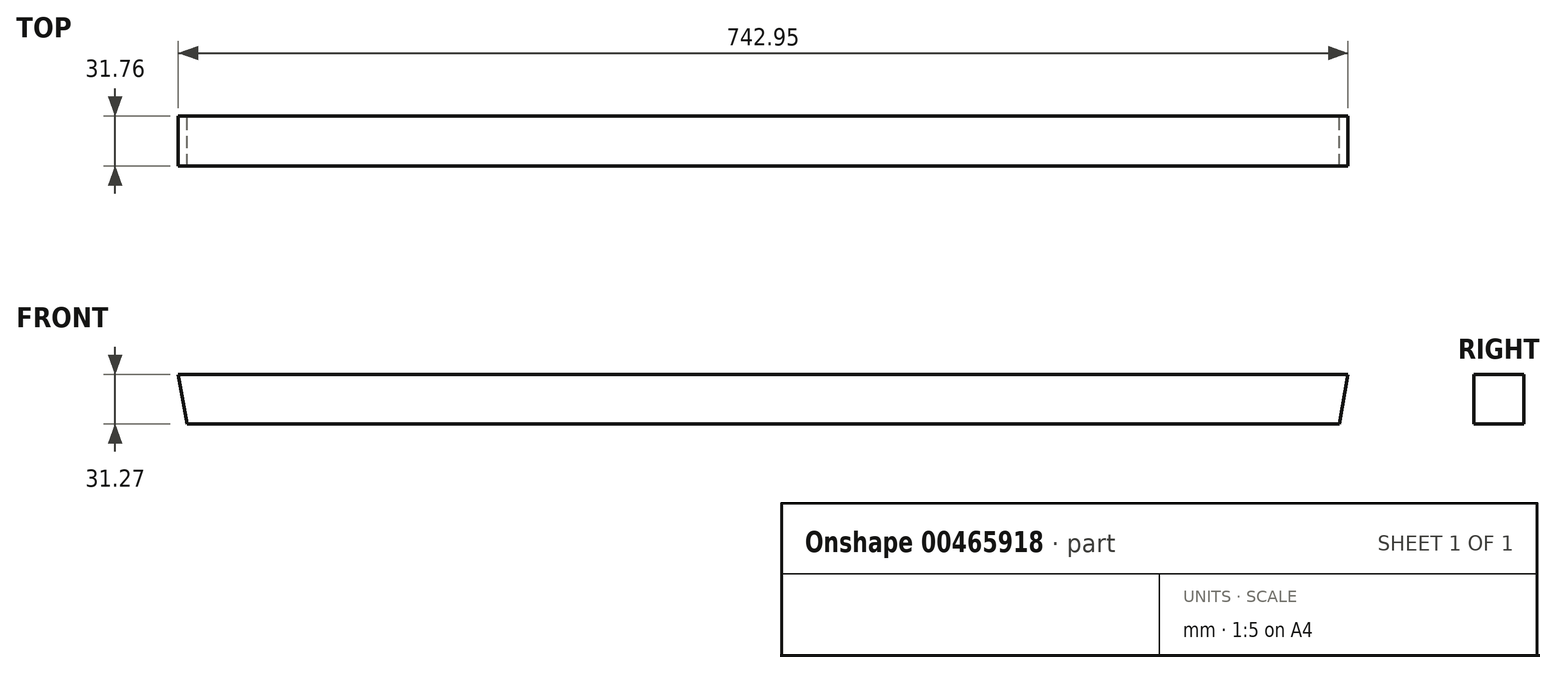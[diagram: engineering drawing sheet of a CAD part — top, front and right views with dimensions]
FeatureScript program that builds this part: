
annotation { "Feature Type Name" : "Feature", "Feature Type Description" : "" }
export const myFeature = defineFeature(function(context is Context, id is Id, definition is map)
    precondition{}
    {
        {
            var Q0;
            Q0=qCreatedBy(makeId("Front.planeOp"),FACE);
            var sketch = newSketch(context, id + "F0", { "sketchPlane" : qUnion([Q0])});
            skLineSegment(sketch, "E0", {"start": v(0, 0) * mm, "end": v(-742.95, 0) * mm});
            skLineSegment(sketch, "E1", {"start": v(-742.95, 0) * mm, "end": v(-737.44, -31.27) * mm});
            skLineSegment(sketch, "E2", {"start": v(0, 0) * mm, "end": v(-5.51, -31.27) * mm});
            skLineSegment(sketch, "E3", {"start": v(-737.44, -31.27) * mm, "end": v(-5.51, -31.27) * mm});
            skSolve(sketch);
        }
        {
            var Q0;
            Q0=makeQuery(id+"F0.imprint","IMPRINT",FACE,{"disambiguationData":[TD([[makeQuery(id+"F0.imprint","IMPRINT",EDGE,{"derivedFrom":sQuery(id+"F0.wireOp",EDGE,"E0")}),1.0]])]});
            extrude(context, id + "F1", {"entities" : qUnion([Q0]), "endBound" : BoundingType.SYMMETRIC, "depth" : 31.75 * mm});
        }
    });
